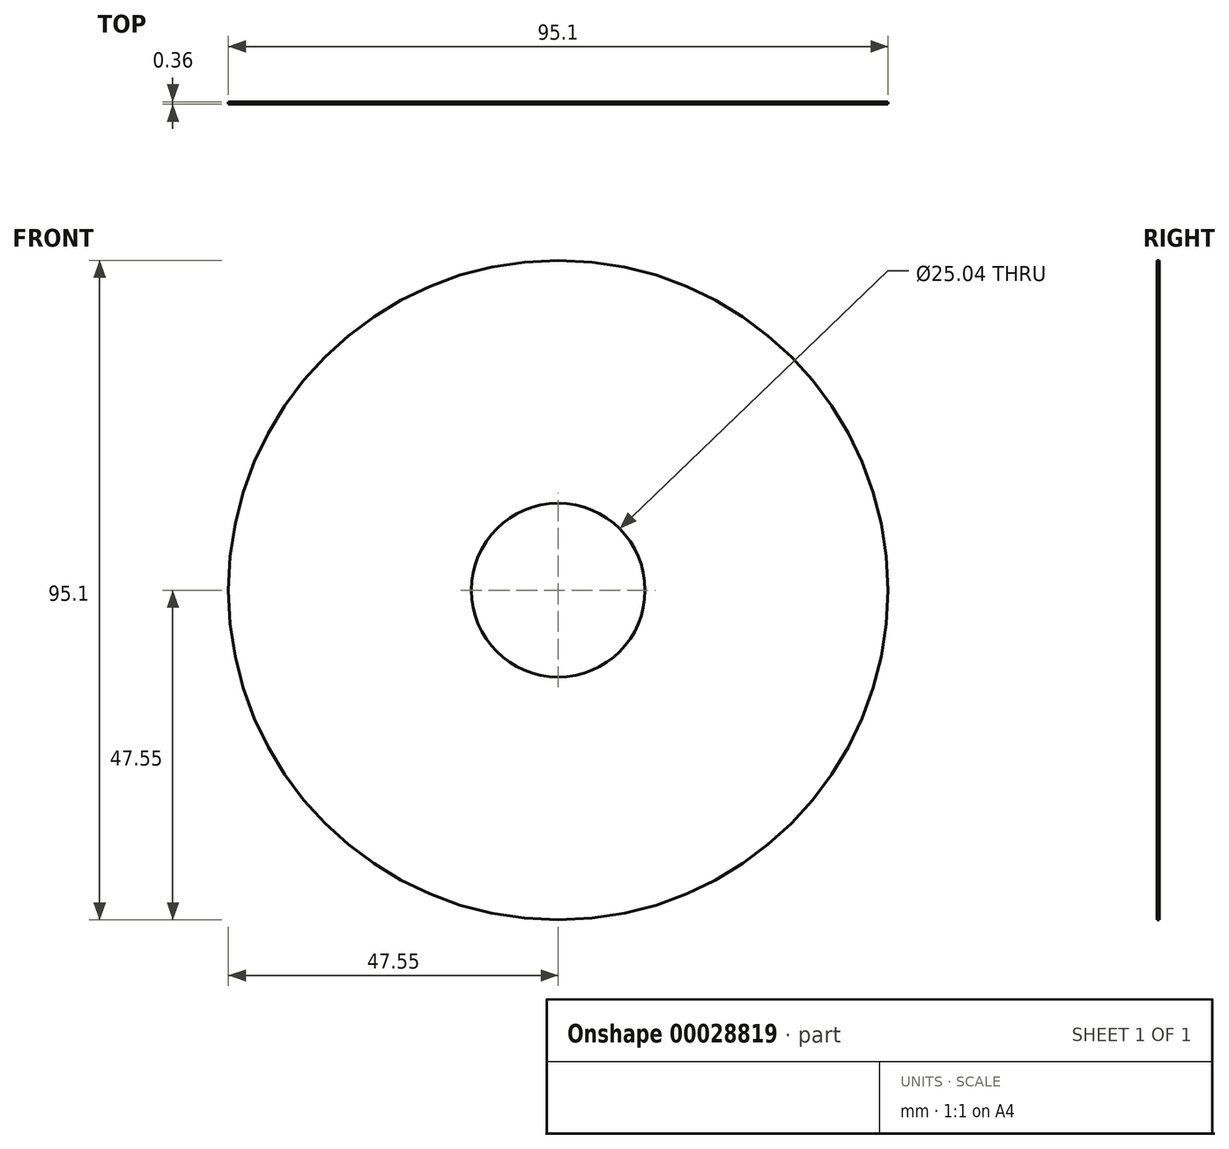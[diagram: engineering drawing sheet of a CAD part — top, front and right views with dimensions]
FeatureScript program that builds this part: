
annotation { "Feature Type Name" : "Feature", "Feature Type Description" : "" }
export const myFeature = defineFeature(function(context is Context, id is Id, definition is map)
    precondition{}
    {
        {
            var Q0;
            Q0=qCreatedBy(makeId("Front.planeOp"),FACE);
            var sketch = newSketch(context, id + "F0", { "sketchPlane" : qUnion([Q0])});
            skCircle(sketch, "E0", {"center": v(0, 0) * mm, "radius": 47.55 * mm});
            skCircle(sketch, "E1", {"center": v(0, 0) * mm, "radius": 12.52 * mm});
            skSolve(sketch);
        }
        {
            var Q0;
            Q0 = qSketchRegion(id + "F0", true);
            extrude(context, id + "F1", {"entities" : qUnion([Q0]), "oppositeDirection" : true, "depth" : 0.36 * mm});
        }
    });
